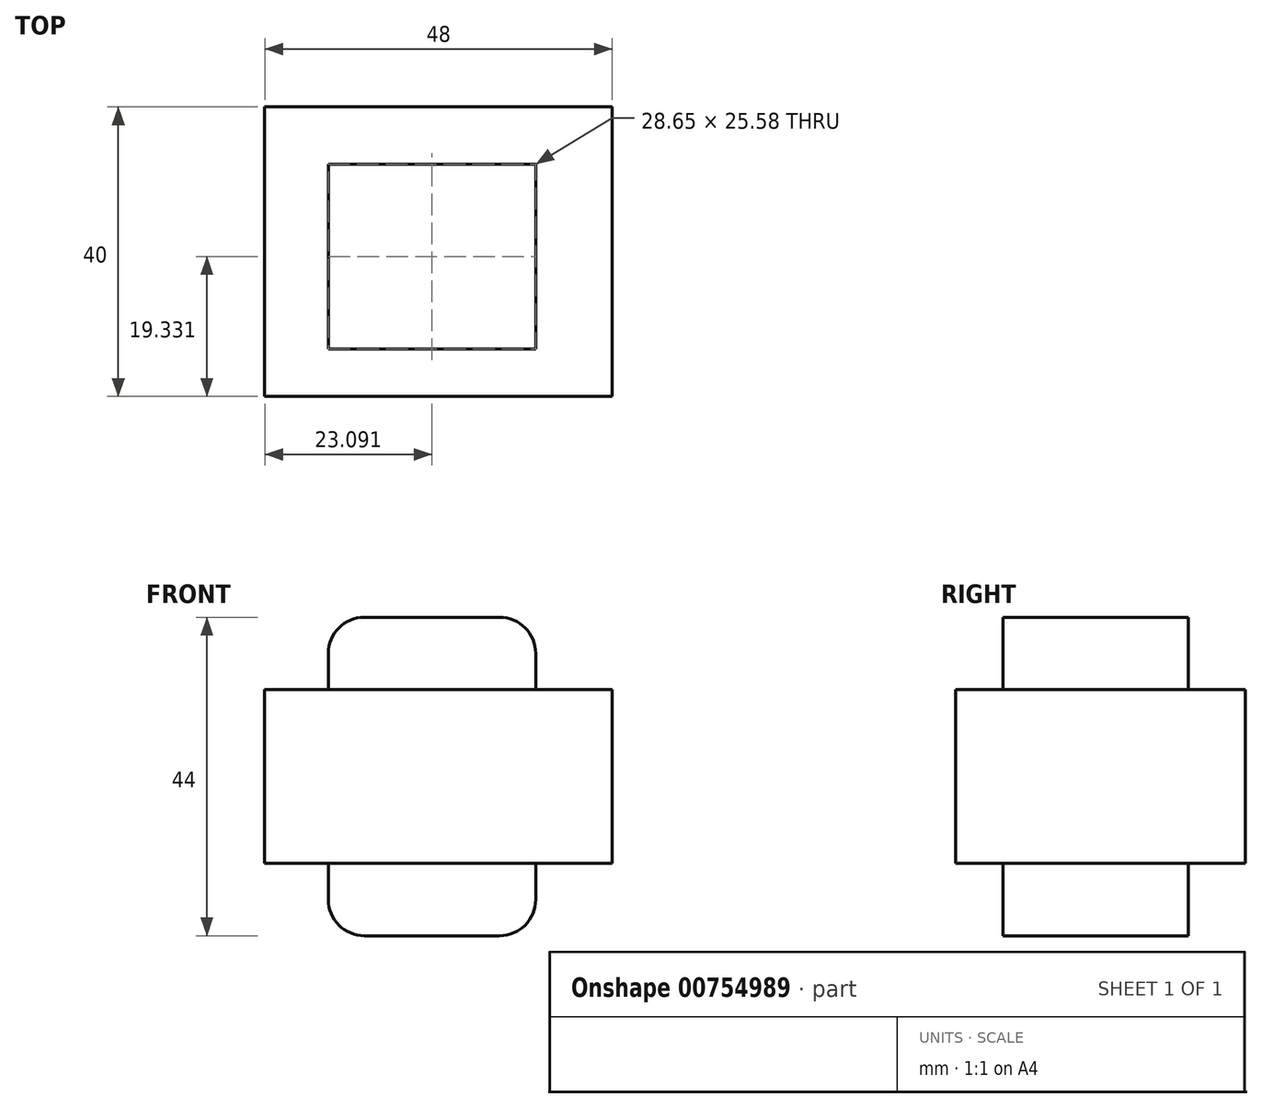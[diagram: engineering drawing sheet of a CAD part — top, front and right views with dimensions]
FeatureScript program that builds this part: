
annotation { "Feature Type Name" : "Feature", "Feature Type Description" : "" }
export const myFeature = defineFeature(function(context is Context, id is Id, definition is map)
    precondition{}
    {
        {
            var Q0;
            Q0=qCreatedBy(makeId("Top.planeOp"),FACE);
            var sketch = newSketch(context, id + "F0", { "sketchPlane" : qUnion([Q0])});
            skLineSegment(sketch, "E0.bottom", {"start": v(-10.88, 11.15) * mm, "end": v(37.12, 11.15) * mm});
            skLineSegment(sketch, "E0.top", {"start": v(-10.88, -28.85) * mm, "end": v(37.12, -28.85) * mm});
            skLineSegment(sketch, "E0.left", {"start": v(-10.88, 11.15) * mm, "end": v(-10.88, -28.85) * mm});
            skLineSegment(sketch, "E0.right", {"start": v(37.12, 11.15) * mm, "end": v(37.12, -28.85) * mm});
            skSolve(sketch);
        }
        {
            var Q0;
            Q0 = qSketchRegion(id + "F0", true);
            extrude(context, id + "F1", {"entities" : qUnion([Q0]), "depth" : 24 * mm, "offsetDistance" : 25 * mm});
        }
        {
            var Q0;
            Q0=makeQuery(id+"F1.opExtrude","CAP_FACE",FACE,{"disambiguationData":[OSD([sQuery(id+"F0.wireOp",EDGE,"E0.bottom"),sQuery(id+"F0.wireOp",EDGE,"E0.top"),sQuery(id+"F0.wireOp",EDGE,"E0.left"),sQuery(id+"F0.wireOp",EDGE,"E0.right")])],"isStart":false});
            var sketch = newSketch(context, id + "F2", { "sketchPlane" : qUnion([Q0])});
            skLineSegment(sketch, "E1.bottom", {"start": v(-2.12, 3.27) * mm, "end": v(26.54, 3.27) * mm});
            skLineSegment(sketch, "E1.top", {"start": v(-2.12, -22.3) * mm, "end": v(26.54, -22.3) * mm});
            skLineSegment(sketch, "E1.left", {"start": v(-2.12, 3.27) * mm, "end": v(-2.12, -22.3) * mm});
            skLineSegment(sketch, "E1.right", {"start": v(26.54, 3.27) * mm, "end": v(26.54, -22.3) * mm});
            skSolve(sketch);
        }
        {
            var Q0;
            Q0 = qSketchRegion(id + "F2", true);
            extrude(context, id + "F3", {"entities" : qUnion([Q0]), "operationType" : NewBodyOperationType.ADD, "depth" : 10 * mm, "offsetDistance" : 25 * mm, "hasSecondDirection" : true, "secondDirectionOppositeDirection" : true, "secondDirectionDepth" : 34 * mm});
        }
        {
            var Q0;
            Q0=makeQuery(id+"F3.opExtrude","CAP_EDGE",EDGE,{"disambiguationData":[OSD([sQuery(id+"F2.wireOp",EDGE,"E1.right")])],"isStart":false});
            var Q1;
            Q1=makeQuery(id+"F3.opExtrude","CAP_EDGE",EDGE,{"disambiguationData":[OSD([sQuery(id+"F2.wireOp",EDGE,"E1.right")])],"isStart":true});
            var Q2;
            Q2=makeQuery(id+"F3.opExtrude","CAP_EDGE",EDGE,{"disambiguationData":[OSD([sQuery(id+"F2.wireOp",EDGE,"E1.left")])],"isStart":true});
            var Q3;
            Q3=makeQuery(id+"F3.opExtrude","CAP_EDGE",EDGE,{"disambiguationData":[OSD([sQuery(id+"F2.wireOp",EDGE,"E1.left")])],"isStart":false});
            fillet(context, id + "F4", {"entities" : qUnion([Q0, Q1, Q2, Q3]), "radius" : 5 * mm, "tangentPropagation" : true, "allowEdgeOverflow" : false});
        }
    });
